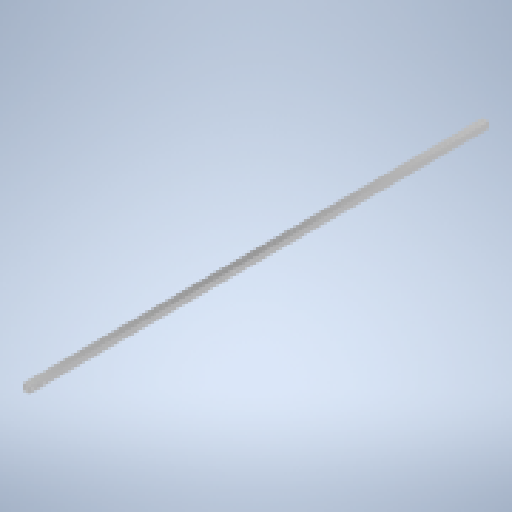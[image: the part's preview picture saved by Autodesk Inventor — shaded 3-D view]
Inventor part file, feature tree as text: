
AUTODESK INVENTOR PART (.ipt)
format: ipt  version: 2024 (Build 280153000, 153)  size: 323,584 bytes
history: native  units: in
note: dims shown in document units (in); Inventor stores cm internally (conversion verified against a paired STEP export)
features: extrude x3, reference x3, other x3, sketch x2, pattern_linear x1
ambient origin geometry x8: Origin, YZ Plane, XZ Plane, XY Plane, X Axis, Y Axis, Z Axis, Center Point
bodies: Solid1 (feature_tree)
feature tree (12):
  extrude  "Extrusion1"  Depth=1.0in
  extrude  "Extrusion2"  Depth=72.0in TaperAngle=0.0deg
  pattern_linear  "Rectangular Pattern2"  Spacing1=0.201in  [1 undecoded]
  extrude  "Extrusion3"  Depth=1.0in
  sketch  "Sketch2"  dims[d0=1.0in d1=1.0in]
  sketch  "Sketch3"  dims[d2=0.09in d3=72.0in d4=0.0in d5=0.201in d6=0.5in d7=0.5in d8=28.3465in d10=1.0in d11=0.3937in d13=1.0in d15=1.0in d16=0.0in d20=28.7402in d22=1.0in d23=0.201in d24=0.5in d25=0.5in d26=1.1811in d28=1.0in d29=0.3937in d31=1.0in d42=0.0in d43=0.0in d17=0.5in d18=0.0344in]
  reference  "Reference1"
  reference  "Reference2"
  reference  "Reference3"
  other  "<userpath>\Documents\CAD\RAI\RAI Full Assembly.iam"
  other  "RAI Full Assembly.iam"
  other  "Top_angled_gusset:2"
note: 1 required parameter value undecoded (feature->parameter linkage not recoverable at this tier; creation-order binding heuristic only, values carry confidence <= 0.55)
